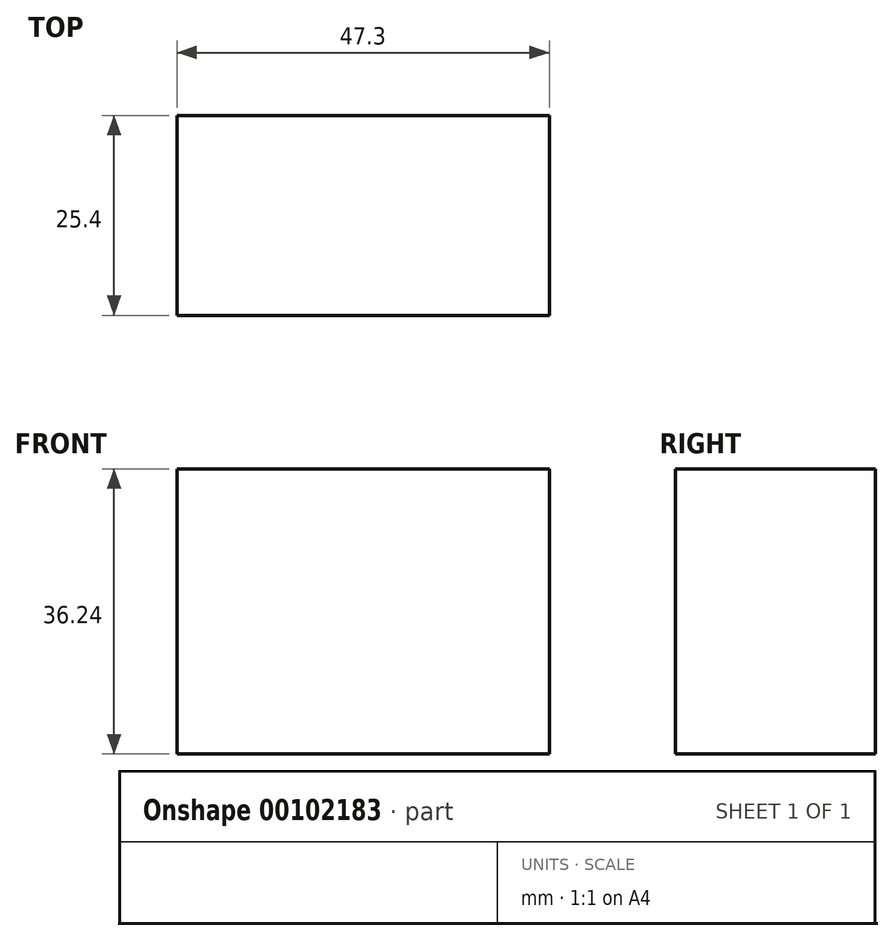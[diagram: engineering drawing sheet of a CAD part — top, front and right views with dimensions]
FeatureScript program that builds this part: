
annotation { "Feature Type Name" : "Feature", "Feature Type Description" : "" }
export const myFeature = defineFeature(function(context is Context, id is Id, definition is map)
    precondition{}
    {
        {
            var Q0;
            Q0=qCreatedBy(makeId("Front.planeOp"),FACE);
            var sketch = newSketch(context, id + "F0", { "sketchPlane" : qUnion([Q0])});
            skLineSegment(sketch, "E0.bottom", {"start": v(23.65, 18.12) * mm, "end": v(-23.65, 18.12) * mm});
            skLineSegment(sketch, "E0.top", {"start": v(23.65, -18.12) * mm, "end": v(-23.65, -18.12) * mm});
            skLineSegment(sketch, "E0.left", {"start": v(23.65, 18.12) * mm, "end": v(23.65, -18.12) * mm});
            skLineSegment(sketch, "E0.right", {"start": v(-23.65, 18.12) * mm, "end": v(-23.65, -18.12) * mm});
            skPoint(sketch, "E0.middle", {"position": v(0, 0) * mm});
            skFitSpline(sketch, "E1", {"points": [v(23.65, 18.12) * mm, v(41.2, 30.7) * mm, v(41.58, 42.53) * mm, v(54.17, 40.63) * mm, v(54.55, 40.63) * mm], "startDerivative": vector(64.87, 26.18) * mm, "endDerivative": vector(3.45, 1.68) * mm});
            skLineSegment(sketch, "E2.MirrorCS", {"start": v(-23.65, 18.12) * mm, "end": v(-23.65, 54.36) * mm});
            skFitSpline(sketch, "E3.MirrorCS", {"points": [v(23.65, 18.12) * mm, v(41.2, 5.53) * mm, v(41.58, -6.3) * mm, v(54.17, -4.39) * mm, v(54.55, -4.39) * mm], "startDerivative": vector(64.87, -26.18) * mm, "endDerivative": vector(3.45, -1.68) * mm});
            skLineSegment(sketch, "E4.MirrorCS", {"start": v(23.65, 54.36) * mm, "end": v(-23.65, 54.36) * mm});
            skSolve(sketch);
        }
        {
            var Q0;
            Q0=makeQuery(id+"F0.imprint","IMPRINT",FACE,{"disambiguationData":[TD([[makeQuery(id+"F0.imprint","IMPRINT",EDGE,{"derivedFrom":sQuery(id+"F0.wireOp",EDGE,"E0.bottom")}),1.0]])]});
            extrude(context, id + "F1", {"entities" : qUnion([Q0]), "oppositeDirection" : true, "depth" : 25.4 * mm});
        }
    });
